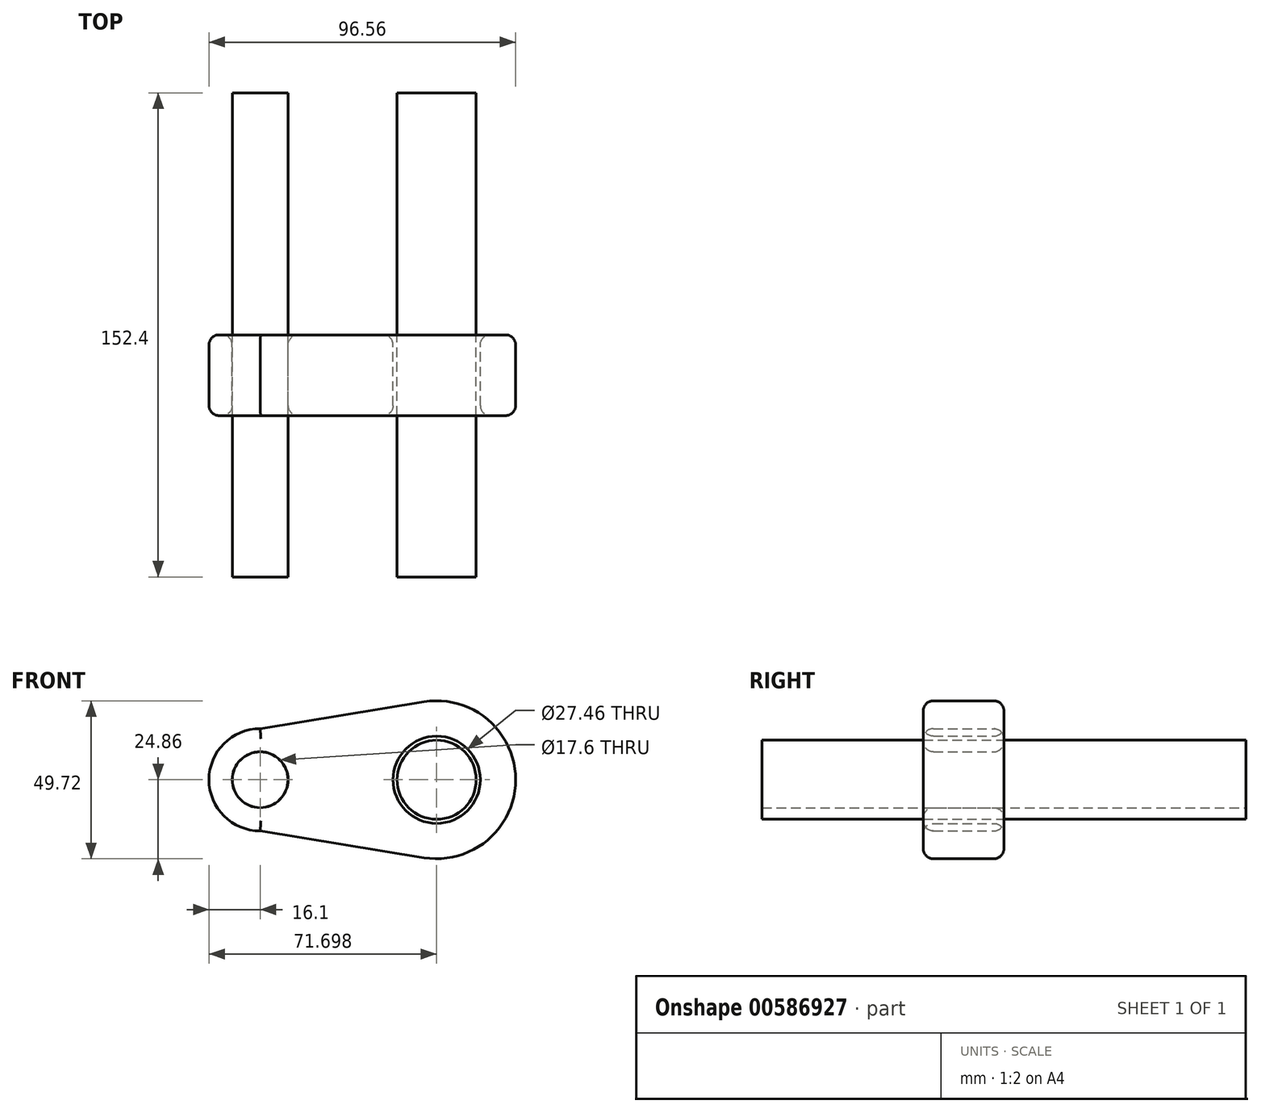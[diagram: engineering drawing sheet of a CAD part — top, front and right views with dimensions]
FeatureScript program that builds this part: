
annotation { "Feature Type Name" : "Feature", "Feature Type Description" : "" }
export const myFeature = defineFeature(function(context is Context, id is Id, definition is map)
    precondition{}
    {
        {
            var Q0;
            Q0=qCreatedBy(makeId("Front.planeOp"),FACE);
            var sketch = newSketch(context, id + "F0", { "sketchPlane" : qUnion([Q0])});
            skCircle(sketch, "E0", {"center": v(0, 0) * mm, "radius": 16.1 * mm});
            skCircle(sketch, "E1", {"center": v(55.6, 0) * mm, "radius": 24.86 * mm});
            skLineSegment(sketch, "E2", {"start": v(0, -16.1) * mm, "end": v(51.6, -24.53) * mm});
            skLineSegment(sketch, "E3", {"start": v(0, 16.1) * mm, "end": v(51.6, 24.53) * mm});
            skCircle(sketch, "E4", {"center": v(0, 0) * mm, "radius": 8.8 * mm});
            skCircle(sketch, "E5", {"center": v(55.6, 0) * mm, "radius": 13.73 * mm});
            skSolve(sketch);
        }
        {
            var Q0;
            {var subQ0=sQuery(id+"F0.wireOp",EDGE,"E2");Q0=makeQuery(id+"F0.imprint","IMPRINT",FACE,{"disambiguationData":[TD([[makeQuery(id+"F0.imprint","IMPRINT",EDGE,{"derivedFrom":subQ0}),1.0]])]});}
            var Q1;
            Q1=makeQuery(id+"F0.imprint","IMPRINT",FACE,{"disambiguationData":[TD([[makeQuery(id+"F0.imprint","IMPRINT",EDGE,{"derivedFrom":sQuery(id+"F0.wireOp",EDGE,"E4")}),-1.0]])]});
            var Q2;
            Q2=makeQuery(id+"F0.imprint","IMPRINT",FACE,{"disambiguationData":[TD([[makeQuery(id+"F0.imprint","IMPRINT",EDGE,{"derivedFrom":sQuery(id+"F0.wireOp",EDGE,"E5")}),-1.0]])]});
            extrude(context, id + "F1", {"entities" : qUnion([Q0, Q1, Q2]), "depth" : 25.4 * mm, "offsetDistance" : 25.4 * mm});
        }
        {
            var Q0;
            Q0=makeQuery(id+"F1.opExtrude","CAP_EDGE",EDGE,{"disambiguationData":[OSD([sQuery(id+"F0.wireOp",EDGE,"E1")])],"isStart":true});
            var Q1;
            Q1=makeQuery(id+"F1.opExtrude","CAP_EDGE",EDGE,{"disambiguationData":[OSD([sQuery(id+"F0.wireOp",EDGE,"E3")])],"isStart":true});
            var Q2;
            Q2=makeQuery(id+"F1.opExtrude","CAP_EDGE",EDGE,{"disambiguationData":[OSD([sQuery(id+"F0.wireOp",EDGE,"E3")])],"isStart":false});
            var Q3;
            Q3=makeQuery(id+"F1.opExtrude","CAP_EDGE",EDGE,{"disambiguationData":[OSD([sQuery(id+"F0.wireOp",EDGE,"E2")])],"isStart":false});
            var Q4;
            Q4=makeQuery(id+"F1.opExtrude","CAP_EDGE",EDGE,{"disambiguationData":[OSD([sQuery(id+"F0.wireOp",EDGE,"E2")])],"isStart":true});
            var Q5;
            Q5=makeQuery(id+"F1.opExtrude","CAP_EDGE",EDGE,{"disambiguationData":[OSD([sQuery(id+"F0.wireOp",EDGE,"E1")])],"isStart":false});
            var Q6;
            Q6=makeQuery(id+"F1.opExtrude","CAP_EDGE",EDGE,{"disambiguationData":[OSD([sQuery(id+"F0.wireOp",EDGE,"E0")])],"isStart":false});
            var Q7;
            Q7=makeQuery(id+"F1.opExtrude","CAP_EDGE",EDGE,{"disambiguationData":[OSD([sQuery(id+"F0.wireOp",EDGE,"E0")])],"isStart":true});
            fillet(context, id + "F2", {"entities" : qUnion([Q0, Q1, Q2, Q3, Q4, Q5, Q6, Q7]), "radius" : 3.17 * mm, "tangentPropagation" : true, "allowEdgeOverflow" : false});
        }
        {
            var Q0;
            Q0=makeQuery(id+"F1.opExtrude","CAP_EDGE",EDGE,{"disambiguationData":[OSD([sQuery(id+"F0.wireOp",EDGE,"E5")])],"isStart":false});
            var Q1;
            Q1=makeQuery(id+"F1.opExtrude","CAP_EDGE",EDGE,{"disambiguationData":[OSD([sQuery(id+"F0.wireOp",EDGE,"E4")])],"isStart":false});
            var Q2;
            Q2=makeQuery(id+"F1.opExtrude","CAP_EDGE",EDGE,{"disambiguationData":[OSD([sQuery(id+"F0.wireOp",EDGE,"E5")])],"isStart":true});
            var Q3;
            Q3=makeQuery(id+"F1.opExtrude","CAP_EDGE",EDGE,{"disambiguationData":[OSD([sQuery(id+"F0.wireOp",EDGE,"E4")])],"isStart":true});
            fillet(context, id + "F3", {"entities" : qUnion([Q0, Q1, Q2, Q3]), "radius" : 3.17 * mm, "tangentPropagation" : true, "allowEdgeOverflow" : false});
        }
        {
            var Q0;
            Q0=qCreatedBy(makeId("Front.planeOp"),FACE);
            var sketch = newSketch(context, id + "F4", { "sketchPlane" : qUnion([Q0])});
            skCircle(sketch, "E6", {"center": v(0, 0) * mm, "radius": 8.78 * mm});
            skSolve(sketch);
        }
        {
            var Q0;
            Q0 = qSketchRegion(id + "F4", true);
            extrude(context, id + "F5", {"entities" : qUnion([Q0]), "depth" : 152.4 * mm, "offsetDistance" : 25.4 * mm, "symmetric" : true});
        }
        {
            var Q0;
            Q0=qCreatedBy(makeId("Front.planeOp"),FACE);
            var sketch = newSketch(context, id + "F6", { "sketchPlane" : qUnion([Q0])});
            skCircle(sketch, "E7", {"center": v(55.6, 0) * mm, "radius": 12.45 * mm});
            skSolve(sketch);
        }
        {
            var Q0;
            Q0=makeQuery(id+"F6.imprint","IMPRINT",FACE,{"disambiguationData":[TD([[makeQuery(id+"F6.imprint","IMPRINT",EDGE,{"derivedFrom":sQuery(id+"F6.wireOp",EDGE,"E7")}),1.0]])]});
            extrude(context, id + "F7", {"entities" : qUnion([Q0]), "depth" : 152.4 * mm, "offsetDistance" : 25.4 * mm, "symmetric" : true});
        }
    });
